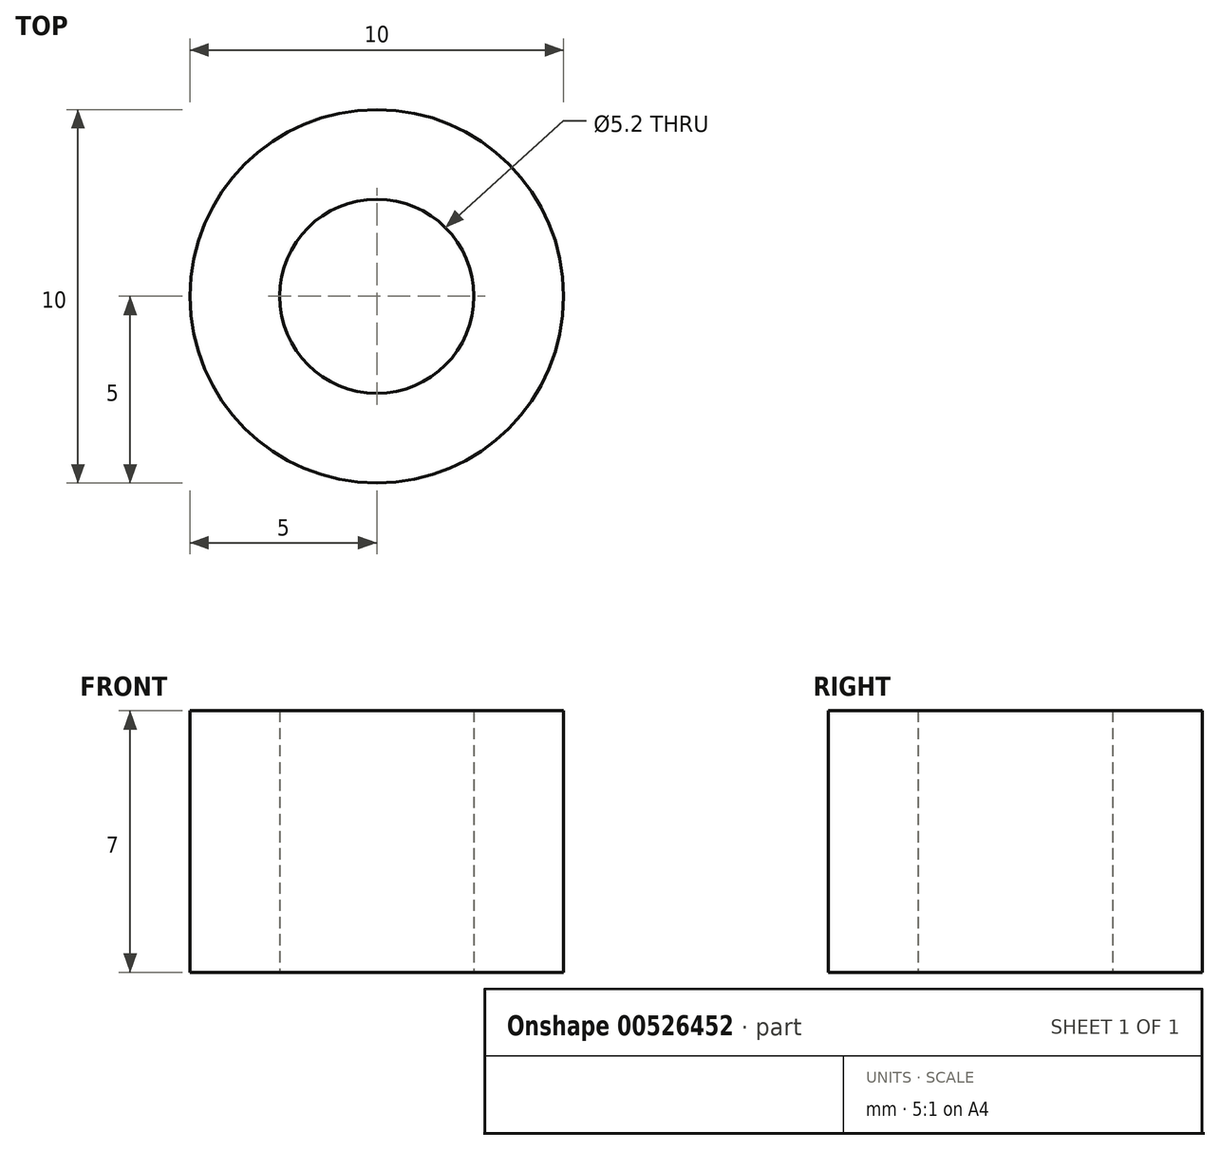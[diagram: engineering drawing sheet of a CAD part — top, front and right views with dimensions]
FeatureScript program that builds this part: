
annotation { "Feature Type Name" : "Feature", "Feature Type Description" : "" }
export const myFeature = defineFeature(function(context is Context, id is Id, definition is map)
    precondition{}
    {
        {
            var Q0;
            Q0=qCreatedBy(makeId("Top.planeOp"),FACE);
            var sketch = newSketch(context, id + "F0", { "sketchPlane" : qUnion([Q0])});
            skCircle(sketch, "E0", {"center": v(0, 0) * mm, "radius": 5 * mm});
            skCircle(sketch, "E1", {"center": v(0, 0) * mm, "radius": 2.6 * mm});
            skSolve(sketch);
        }
        {
            var Q0;
            Q0 = qSketchRegion(id + "F0", true);
            extrude(context, id + "F1", {"entities" : qUnion([Q0]), "depth" : 7 * mm, "offsetDistance" : 25 * mm});
        }
    });
